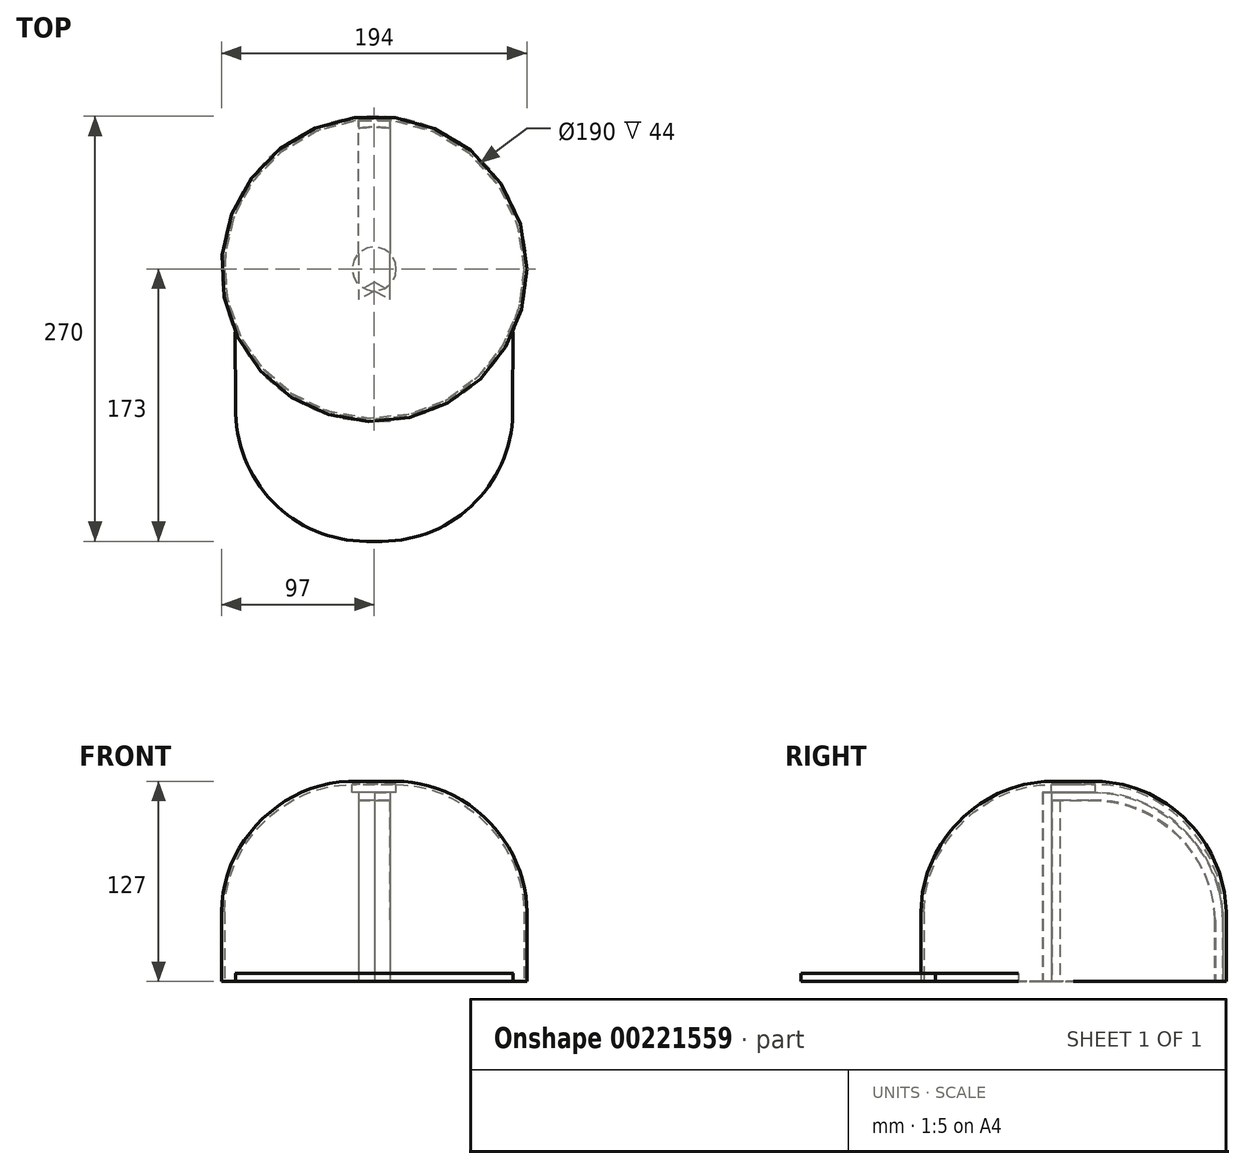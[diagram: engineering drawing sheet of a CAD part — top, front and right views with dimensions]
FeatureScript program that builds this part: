
annotation { "Feature Type Name" : "Feature", "Feature Type Description" : "" }
export const myFeature = defineFeature(function(context is Context, id is Id, definition is map)
    precondition{}
    {
        {
            var Q0;
            Q0=qCreatedBy(makeId("Top.planeOp"),FACE);
            var sketch = newSketch(context, id + "F0", { "sketchPlane" : qUnion([Q0])});
            skCircle(sketch, "E0", {"center": v(0, 0) * mm, "radius": 95 * mm});
            skLineSegment(sketch, "E1", {"start": v(0, -95) * mm, "end": v(0, -35) * mm});
            skLineSegment(sketch, "E2", {"start": v(0, -95) * mm, "end": v(0, -173) * mm});
            skLineSegment(sketch, "E3", {"start": v(0, -173) * mm, "end": v(5, -173) * mm});
            skPoint(sketch, "E4.visualSharp", {"position": v(95, -173) * mm});
            skArc(sketch, "E4.filletArc", {"start": v(5, -173) * mm, "mid": v(64.5, -147.88) * mm, "end": v(87.97, -87.71) * mm});
            skLineSegment(sketch, "E5", {"start": v(87.97, -87.71) * mm, "end": v(88.32, -35) * mm});
            skPoint(sketch, "E6.MirrorP", {"position": v(-95, -173) * mm});
            skLineSegment(sketch, "E7.MirrorCS", {"start": v(-87.97, -87.71) * mm, "end": v(-88.32, -35) * mm});
            skArc(sketch, "E8.MirrorCS", {"start": v(-5, -173) * mm, "mid": v(-64.5, -147.88) * mm, "end": v(-87.97, -87.71) * mm});
            skLineSegment(sketch, "E9.MirrorCS", {"start": v(0, -173) * mm, "end": v(-5, -173) * mm});
            skLineSegment(sketch, "E10", {"start": v(0, 95) * mm, "end": v(0, 0) * mm});
            skLineSegment(sketch, "E11", {"start": v(-85.03, 42.37) * mm, "end": v(0, 0) * mm});
            skLineSegment(sketch, "E12", {"start": v(-82.22, -47.59) * mm, "end": v(0, 0) * mm});
            skLineSegment(sketch, "E13", {"start": v(0, -95) * mm, "end": v(0, 0) * mm});
            skLineSegment(sketch, "E14.MirrorCS", {"start": v(85.03, 42.37) * mm, "end": v(0, 0) * mm});
            skLineSegment(sketch, "E15.MirrorCS", {"start": v(82.22, -47.59) * mm, "end": v(0, 0) * mm});
            skSolve(sketch);
        }
        {
            var Q0;
            {var subQ3=sQuery(id+"F0.wireOp",EDGE,"E12");Q0=makeQuery(id+"F0.imprint","IMPRINT",FACE,{"disambiguationData":[TD([[makeQuery(id+"F0.imprint","IMPRINT",EDGE,{"derivedFrom":subQ3}),-1.0]])]});}
            var Q1;
            {var subQ2=sQuery(id+"F0.wireOp",EDGE,"E11");Q1=makeQuery(id+"F0.imprint","IMPRINT",FACE,{"disambiguationData":[TD([[makeQuery(id+"F0.imprint","IMPRINT",EDGE,{"derivedFrom":subQ2}),-1.0]])]});}
            var Q2;
            {var subQ0=sQuery(id+"F0.wireOp",EDGE,"E10");Q2=makeQuery(id+"F0.imprint","IMPRINT",FACE,{"disambiguationData":[TD([[makeQuery(id+"F0.imprint","IMPRINT",EDGE,{"derivedFrom":subQ0}),-1.0]])]});}
            var Q3;
            {var subQ0=sQuery(id+"F0.wireOp",EDGE,"E10");Q3=makeQuery(id+"F0.imprint","IMPRINT",FACE,{"disambiguationData":[TD([[makeQuery(id+"F0.imprint","IMPRINT",EDGE,{"derivedFrom":subQ0}),1.0]])]});}
            var Q4;
            {var subQ3=sQuery(id+"F0.wireOp",EDGE,"E14.MirrorCS");Q4=makeQuery(id+"F0.imprint","IMPRINT",FACE,{"disambiguationData":[TD([[makeQuery(id+"F0.imprint","IMPRINT",EDGE,{"derivedFrom":subQ3}),1.0]])]});}
            var Q5;
            {var subQ3=sQuery(id+"F0.wireOp",EDGE,"E15.MirrorCS");Q5=makeQuery(id+"F0.imprint","IMPRINT",FACE,{"disambiguationData":[TD([[makeQuery(id+"F0.imprint","IMPRINT",EDGE,{"derivedFrom":subQ3}),1.0]])]});}
            extrude(context, id + "F1", {"entities" : qUnion([Q0, Q1, Q2, Q3, Q4, Q5]), "depth" : 125 * mm});
        }
        {
            var Q0;
            Q0=makeQuery(id+"F1.opExtrude","CAP_EDGE",EDGE,{"disambiguationData":[OSD([sQuery(id+"F0.wireOp",EDGE,"E0")])],"isStart":false});
            fillet(context, id + "F2", {"entities" : qUnion([Q0]), "radius" : 81 * mm, "tangentPropagation" : true, "rho" : 0.4, "crossSection" : FilletCrossSection.CONIC, "allowEdgeOverflow" : false});
        }
        {
            var Q0;
            {var subQ1=sQuery(id+"F0.wireOp",EDGE,"E2");Q0=makeQuery(id+"F0.imprint","IMPRINT",FACE,{"disambiguationData":[TD([[makeQuery(id+"F0.imprint","IMPRINT",EDGE,{"derivedFrom":subQ1}),-1.0]])]});}
            var Q1;
            {var subQ0=sQuery(id+"F0.wireOp",EDGE,"E2");Q1=makeQuery(id+"F0.imprint","IMPRINT",FACE,{"disambiguationData":[TD([[makeQuery(id+"F0.imprint","IMPRINT",EDGE,{"derivedFrom":subQ0}),1.0]])]});}
            extrude(context, id + "F3", {"entities" : qUnion([Q0, Q1]), "depth" : 5 * mm});
        }
        {
            var Q0;
            Q0=makeQuery(id+"F1.opExtrude","CAP_FACE",FACE,{"disambiguationData":[OSD([sQuery(id+"F0.wireOp",EDGE,"E0")])],"isStart":true});
            shell(context, id + "F4", {"entities" : qUnion([Q0]), "thickness" : 2 * mm, "oppositeDirection" : true});
        }
        {
            var Q0;
            {var subQ0=sQuery(id+"F0.wireOp",EDGE,"E0");Q0=makeQuery(id+"F4.opShell","OFFSET_FACE",FACE,{"disambiguationData":[OSD([subQ0]),TDD([makeQuery(id+"F1.opExtrude","CAP_FACE",FACE,{"disambiguationData":[OSD([subQ0])],"isStart":false})])]});}
            extrude(context, id + "F5", {"entities" : qUnion([Q0]), "depth" : 5 * mm});
        }
        {
            var Q0;
            Q0=qCreatedBy(makeId("Top.planeOp"),FACE);
            var sketch = newSketch(context, id + "F6", { "sketchPlane" : qUnion([Q0])});
            skCircle(sketch, "E16", {"center": v(0, 0) * mm, "radius": 95 * mm});
            skLineSegment(sketch, "E17", {"start": v(0, -95) * mm, "end": v(0, -35) * mm});
            skLineSegment(sketch, "E18", {"start": v(0, -95) * mm, "end": v(0, -173) * mm});
            skLineSegment(sketch, "E19", {"start": v(0, -173) * mm, "end": v(5, -173) * mm});
            skPoint(sketch, "E20.visualSharp", {"position": v(95, -173) * mm});
            skArc(sketch, "E20.filletArc", {"start": v(5, -173) * mm, "mid": v(64.5, -147.88) * mm, "end": v(87.97, -87.71) * mm});
            skLineSegment(sketch, "E21", {"start": v(87.97, -87.71) * mm, "end": v(88.32, -35) * mm});
            skPoint(sketch, "E22.MirrorP", {"position": v(-95, -173) * mm});
            skLineSegment(sketch, "E23.MirrorCS", {"start": v(-87.97, -87.71) * mm, "end": v(-88.32, -35) * mm});
            skArc(sketch, "E24.MirrorCS", {"start": v(-5, -173) * mm, "mid": v(-64.5, -147.88) * mm, "end": v(-87.97, -87.71) * mm});
            skLineSegment(sketch, "E25.MirrorCS", {"start": v(0, -173) * mm, "end": v(-5, -173) * mm});
            skLineSegment(sketch, "E26", {"start": v(0, 95) * mm, "end": v(0, 0) * mm});
            skLineSegment(sketch, "E27", {"start": v(-85.03, 42.37) * mm, "end": v(0, 0) * mm});
            skLineSegment(sketch, "E28", {"start": v(-82.22, -47.59) * mm, "end": v(0, 0) * mm});
            skLineSegment(sketch, "E29", {"start": v(0, -95) * mm, "end": v(0, 0) * mm});
            skLineSegment(sketch, "E30.MirrorCS", {"start": v(85.03, 42.37) * mm, "end": v(0, 0) * mm});
            skLineSegment(sketch, "E31.MirrorCS", {"start": v(82.22, -47.59) * mm, "end": v(0, 0) * mm});
            skLineSegment(sketch, "E32", {"start": v(-88.77, 33.85) * mm, "end": v(77, -55.64) * mm});
            skLineSegment(sketch, "E33", {"start": v(-79.71, 51.68) * mm, "end": v(86.94, -38.3) * mm});
            skLineSegment(sketch, "E34", {"start": v(86.94, -38.3) * mm, "end": v(77, -55.64) * mm});
            skLineSegment(sketch, "E35", {"start": v(-88.77, 33.85) * mm, "end": v(-79.71, 51.68) * mm});
            skLineSegment(sketch, "E36", {"start": v(88.82, 33.71) * mm, "end": v(-76.93, -55.74) * mm});
            skLineSegment(sketch, "E37", {"start": v(79.8, 51.56) * mm, "end": v(-86.9, -38.4) * mm});
            skLineSegment(sketch, "E38", {"start": v(79.8, 51.56) * mm, "end": v(88.82, 33.71) * mm});
            skLineSegment(sketch, "E39", {"start": v(-76.93, -55.74) * mm, "end": v(-86.9, -38.4) * mm});
            skLineSegment(sketch, "E40", {"start": v(-10, 94.47) * mm, "end": v(-10, -94.47) * mm});
            skLineSegment(sketch, "E41", {"start": v(-10, -94.47) * mm, "end": v(10, -94.47) * mm});
            skLineSegment(sketch, "E42", {"start": v(10, -94.47) * mm, "end": v(10, 94.47) * mm});
            skLineSegment(sketch, "E43", {"start": v(10, 94.47) * mm, "end": v(-10, 94.47) * mm});
            skSolve(sketch);
        }
        {
            var Q0;
            {var subQ0=sQuery(id+"F6.wireOp",EDGE,"E43");var subQ1=sQuery(id+"F6.wireOp",EDGE,"E26");var subQ2=makeQuery(id+"F6.imprint","INTERSECT",VERTEX,{"derivedFrom":[subQ1,subQ0]});Q0=makeQuery(id+"F6.imprint","IMPRINT",FACE,{"disambiguationData":[TD([[makeQuery(id+"F6.imprint","IMPRINT",EDGE,{"disambiguationData":[TD([[subQ2,-1.0]])],"derivedFrom":subQ1}),-1.0]])]});}
            var Q1;
            {var subQ0=sQuery(id+"F6.wireOp",EDGE,"E43");var subQ7=sQuery(id+"F6.wireOp",EDGE,"E26");var subQ9=makeQuery(id+"F6.imprint","INTERSECT",VERTEX,{"derivedFrom":[subQ7,subQ0]});Q1=makeQuery(id+"F6.imprint","IMPRINT",FACE,{"disambiguationData":[TD([[makeQuery(id+"F6.imprint","IMPRINT",EDGE,{"disambiguationData":[TD([[subQ9,-1.0]])],"derivedFrom":subQ7}),1.0]])]});}
            var Q2;
            {var subQ5=sQuery(id+"F6.wireOp",EDGE,"E29");var subQ7=makeQuery(id+"F6.imprint","IMPRINT",VERTEX,{"derivedFrom":subQ5});Q2=makeQuery(id+"F6.imprint","IMPRINT",FACE,{"disambiguationData":[TD([[makeQuery(id+"F6.imprint","IMPRINT",EDGE,{"disambiguationData":[TD([[subQ7,1.0]])],"derivedFrom":subQ5}),-1.0]])]});}
            var Q3;
            {var subQ5=sQuery(id+"F6.wireOp",EDGE,"E29");var subQ7=makeQuery(id+"F6.imprint","IMPRINT",VERTEX,{"derivedFrom":subQ5});Q3=makeQuery(id+"F6.imprint","IMPRINT",FACE,{"disambiguationData":[TD([[makeQuery(id+"F6.imprint","IMPRINT",EDGE,{"disambiguationData":[TD([[subQ7,1.0]])],"derivedFrom":subQ5}),1.0]])]});}
            var Q4;
            {var subQ0=sQuery(id+"F6.wireOp",EDGE,"E26");var subQ1=sQuery(id+"F6.wireOp",EDGE,"E16");var subQ2=makeQuery(id+"F6.imprint","INTERSECT",VERTEX,{"derivedFrom":[subQ1,subQ0]});Q4=makeQuery(id+"F6.imprint","IMPRINT",FACE,{"disambiguationData":[TD([[makeQuery(id+"F6.imprint","IMPRINT",EDGE,{"disambiguationData":[TD([[subQ2,-1.0]])],"derivedFrom":subQ0}),1.0]])]});}
            var Q5;
            {var subQ0=sQuery(id+"F6.wireOp",EDGE,"E26");var subQ1=sQuery(id+"F6.wireOp",EDGE,"E16");var subQ2=makeQuery(id+"F6.imprint","INTERSECT",VERTEX,{"derivedFrom":[subQ1,subQ0]});Q5=makeQuery(id+"F6.imprint","IMPRINT",FACE,{"disambiguationData":[TD([[makeQuery(id+"F6.imprint","IMPRINT",EDGE,{"disambiguationData":[TD([[subQ2,-1.0]])],"derivedFrom":subQ0}),-1.0]])]});}
            var Q6;
            {var subQ0=sQuery(id+"F6.wireOp",EDGE,"E29");var subQ3=sQuery(id+"F6.wireOp",EDGE,"E41");var subQ5=makeQuery(id+"F6.imprint","INTERSECT",VERTEX,{"derivedFrom":[subQ0,subQ3]});Q6=makeQuery(id+"F6.imprint","IMPRINT",FACE,{"disambiguationData":[TD([[makeQuery(id+"F6.imprint","IMPRINT",EDGE,{"disambiguationData":[TD([[subQ5,1.0]])],"derivedFrom":subQ0}),1.0]])]});}
            var Q7;
            {var subQ0=sQuery(id+"F6.wireOp",EDGE,"E29");var subQ3=sQuery(id+"F6.wireOp",EDGE,"E41");var subQ5=makeQuery(id+"F6.imprint","INTERSECT",VERTEX,{"derivedFrom":[subQ0,subQ3]});Q7=makeQuery(id+"F6.imprint","IMPRINT",FACE,{"disambiguationData":[TD([[makeQuery(id+"F6.imprint","IMPRINT",EDGE,{"disambiguationData":[TD([[subQ5,1.0]])],"derivedFrom":subQ0}),-1.0]])]});}
            var Q8;
            {var subQ0=sQuery(id+"F6.wireOp",EDGE,"E42");var subQ1=sQuery(id+"F6.wireOp",EDGE,"E30.MirrorCS");var subQ2=makeQuery(id+"F6.imprint","INTERSECT",VERTEX,{"derivedFrom":[subQ1,subQ0]});Q8=makeQuery(id+"F6.imprint","IMPRINT",FACE,{"disambiguationData":[TD([[makeQuery(id+"F6.imprint","IMPRINT",EDGE,{"disambiguationData":[TD([[subQ2,-1.0]])],"derivedFrom":subQ1}),-1.0]])]});}
            var Q9;
            {var subQ0=sQuery(id+"F6.wireOp",EDGE,"E30.MirrorCS");var subQ5=sQuery(id+"F6.wireOp",EDGE,"E33");var subQ6=makeQuery(id+"F6.imprint","INTERSECT",VERTEX,{"derivedFrom":[subQ0,subQ5]});Q9=makeQuery(id+"F6.imprint","IMPRINT",FACE,{"disambiguationData":[TD([[makeQuery(id+"F6.imprint","IMPRINT",EDGE,{"disambiguationData":[TD([[subQ6,1.0]])],"derivedFrom":subQ5}),-1.0]])]});}
            var Q10;
            {var subQ1=sQuery(id+"F6.wireOp",EDGE,"E26");var subQ3=sQuery(id+"F6.wireOp",EDGE,"E37");var subQ4=makeQuery(id+"F6.imprint","INTERSECT",VERTEX,{"derivedFrom":[subQ1,subQ3]});Q10=makeQuery(id+"F6.imprint","IMPRINT",FACE,{"disambiguationData":[TD([[makeQuery(id+"F6.imprint","IMPRINT",EDGE,{"disambiguationData":[TD([[subQ4,-1.0]])],"derivedFrom":subQ3}),1.0]])]});}
            var Q11;
            {var subQ1=sQuery(id+"F6.wireOp",EDGE,"E26");var subQ5=sQuery(id+"F6.wireOp",EDGE,"E33");var subQ6=makeQuery(id+"F6.imprint","INTERSECT",VERTEX,{"derivedFrom":[subQ1,subQ5]});Q11=makeQuery(id+"F6.imprint","IMPRINT",FACE,{"disambiguationData":[TD([[makeQuery(id+"F6.imprint","IMPRINT",EDGE,{"disambiguationData":[TD([[subQ6,-1.0]])],"derivedFrom":subQ1}),-1.0]])]});}
            var Q12;
            {var subQ0=sQuery(id+"F6.wireOp",EDGE,"E36");var subQ1=sQuery(id+"F6.wireOp",EDGE,"E32");var subQ2=makeQuery(id+"F6.imprint","INTERSECT",VERTEX,{"derivedFrom":[subQ1,subQ0]});Q12=makeQuery(id+"F6.imprint","IMPRINT",FACE,{"disambiguationData":[TD([[makeQuery(id+"F6.imprint","IMPRINT",EDGE,{"disambiguationData":[TD([[subQ2,-1.0]])],"derivedFrom":subQ1}),1.0]])]});}
            var Q13;
            {var subQ0=sQuery(id+"F6.wireOp",EDGE,"E36");var subQ1=sQuery(id+"F6.wireOp",EDGE,"E29");var subQ2=makeQuery(id+"F6.imprint","INTERSECT",VERTEX,{"derivedFrom":[subQ1,subQ0]});Q13=makeQuery(id+"F6.imprint","IMPRINT",FACE,{"disambiguationData":[TD([[makeQuery(id+"F6.imprint","IMPRINT",EDGE,{"disambiguationData":[TD([[subQ2,-1.0]])],"derivedFrom":subQ1}),1.0]])]});}
            var Q14;
            {var subQ0=sQuery(id+"F6.wireOp",EDGE,"E29");var subQ5=sQuery(id+"F6.wireOp",EDGE,"E32");var subQ6=makeQuery(id+"F6.imprint","INTERSECT",VERTEX,{"derivedFrom":[subQ0,subQ5]});Q14=makeQuery(id+"F6.imprint","IMPRINT",FACE,{"disambiguationData":[TD([[makeQuery(id+"F6.imprint","IMPRINT",EDGE,{"disambiguationData":[TD([[subQ6,1.0]])],"derivedFrom":subQ5}),1.0]])]});}
            var Q15;
            {var subQ0=sQuery(id+"F6.wireOp",EDGE,"E32");var subQ1=sQuery(id+"F6.wireOp",EDGE,"E29");var subQ2=makeQuery(id+"F6.imprint","INTERSECT",VERTEX,{"derivedFrom":[subQ1,subQ0]});Q15=makeQuery(id+"F6.imprint","IMPRINT",FACE,{"disambiguationData":[TD([[makeQuery(id+"F6.imprint","IMPRINT",EDGE,{"disambiguationData":[TD([[subQ2,-1.0]])],"derivedFrom":subQ0}),1.0]])]});}
            var Q16;
            {var subQ1=sQuery(id+"F6.wireOp",EDGE,"E30.MirrorCS");var subQ3=sQuery(id+"F6.wireOp",EDGE,"E33");var subQ4=makeQuery(id+"F6.imprint","INTERSECT",VERTEX,{"derivedFrom":[subQ1,subQ3]});Q16=makeQuery(id+"F6.imprint","IMPRINT",FACE,{"disambiguationData":[TD([[makeQuery(id+"F6.imprint","IMPRINT",EDGE,{"disambiguationData":[TD([[subQ4,-1.0]])],"derivedFrom":subQ3}),-1.0]])]});}
            var Q17;
            {var subQ1=sQuery(id+"F6.wireOp",EDGE,"E27");var subQ3=sQuery(id+"F6.wireOp",EDGE,"E37");var subQ4=makeQuery(id+"F6.imprint","INTERSECT",VERTEX,{"derivedFrom":[subQ1,subQ3]});Q17=makeQuery(id+"F6.imprint","IMPRINT",FACE,{"disambiguationData":[TD([[makeQuery(id+"F6.imprint","IMPRINT",EDGE,{"disambiguationData":[TD([[subQ4,-1.0]])],"derivedFrom":subQ3}),1.0]])]});}
            var Q18;
            {var subQ0=sQuery(id+"F6.wireOp",EDGE,"E40");var subQ1=sQuery(id+"F6.wireOp",EDGE,"E27");var subQ2=makeQuery(id+"F6.imprint","INTERSECT",VERTEX,{"derivedFrom":[subQ1,subQ0]});Q18=makeQuery(id+"F6.imprint","IMPRINT",FACE,{"disambiguationData":[TD([[makeQuery(id+"F6.imprint","IMPRINT",EDGE,{"disambiguationData":[TD([[subQ2,-1.0]])],"derivedFrom":subQ1}),-1.0]])]});}
            var Q19;
            {var subQ0=sQuery(id+"F6.wireOp",EDGE,"E42");var subQ1=sQuery(id+"F6.wireOp",EDGE,"E30.MirrorCS");var subQ2=makeQuery(id+"F6.imprint","INTERSECT",VERTEX,{"derivedFrom":[subQ1,subQ0]});Q19=makeQuery(id+"F6.imprint","IMPRINT",FACE,{"disambiguationData":[TD([[makeQuery(id+"F6.imprint","IMPRINT",EDGE,{"disambiguationData":[TD([[subQ2,-1.0]])],"derivedFrom":subQ1}),1.0]])]});}
            var Q20;
            {var subQ0=sQuery(id+"F6.wireOp",EDGE,"E36");var subQ1=sQuery(id+"F6.wireOp",EDGE,"E29");var subQ2=makeQuery(id+"F6.imprint","INTERSECT",VERTEX,{"derivedFrom":[subQ1,subQ0]});Q20=makeQuery(id+"F6.imprint","IMPRINT",FACE,{"disambiguationData":[TD([[makeQuery(id+"F6.imprint","IMPRINT",EDGE,{"disambiguationData":[TD([[subQ2,-1.0]])],"derivedFrom":subQ1}),-1.0]])]});}
            var Q21;
            {var subQ0=sQuery(id+"F6.wireOp",EDGE,"E33");var subQ1=sQuery(id+"F6.wireOp",EDGE,"E26");var subQ2=makeQuery(id+"F6.imprint","INTERSECT",VERTEX,{"derivedFrom":[subQ1,subQ0]});Q21=makeQuery(id+"F6.imprint","IMPRINT",FACE,{"disambiguationData":[TD([[makeQuery(id+"F6.imprint","IMPRINT",EDGE,{"disambiguationData":[TD([[subQ2,-1.0]])],"derivedFrom":subQ1}),1.0]])]});}
            extrude(context, id + "F7", {"entities" : qUnion([Q0, Q1, Q2, Q3, Q4, Q5, Q6, Q7, Q8, Q9, Q10, Q11, Q12, Q13, Q14, Q15, Q16, Q17, Q18, Q19, Q20, Q21]), "depth" : 120 * mm});
        }
        {
            var Q0;
            {var subQ0=sQuery(id+"F6.wireOp",EDGE,"E16");var subQ1=makeQuery(id+"F6.imprint","INTERSECT",VERTEX,{"derivedFrom":[subQ0,sQuery(id+"F6.wireOp",EDGE,"E26")]});Q0=makeQuery(id+"F7.opExtrude","CAP_EDGE",EDGE,{"disambiguationData":[OSD([subQ0]),TDD([makeQuery(id+"F6.imprint","IMPRINT",EDGE,{"disambiguationData":[TD([[subQ1,1.0]])],"derivedFrom":subQ0}),makeQuery(id+"F6.imprint","IMPRINT",EDGE,{"disambiguationData":[TD([[subQ1,-1.0]])],"derivedFrom":subQ0})])],"isStart":false});}
            var Q1;
            {var subQ0=sQuery(id+"F6.wireOp",EDGE,"E16");var subQ1=makeQuery(id+"F6.imprint","INTERSECT",VERTEX,{"derivedFrom":[subQ0,sQuery(id+"F6.wireOp",EDGE,"E18"),sQuery(id+"F6.wireOp",EDGE,"E29")]});Q1=makeQuery(id+"F7.opExtrude","CAP_EDGE",EDGE,{"disambiguationData":[OSD([subQ0]),TDD([makeQuery(id+"F6.imprint","IMPRINT",EDGE,{"disambiguationData":[TD([[subQ1,1.0]])],"derivedFrom":subQ0}),makeQuery(id+"F6.imprint","IMPRINT",EDGE,{"disambiguationData":[TD([[subQ1,-1.0]])],"derivedFrom":subQ0})])],"isStart":false});}
            fillet(context, id + "F8", {"entities" : qUnion([Q0, Q1]), "radius" : 81 * mm, "tangentPropagation" : true, "rho" : 0.4, "crossSection" : FilletCrossSection.CONIC, "allowEdgeOverflow" : false});
        }
        {
            var Q0;
            Q0=makeQuery(id+"F7.opExtrude","SWEPT_FACE",FACE,{"disambiguationData":[OSD([sQuery(id+"F6.wireOp",EDGE,"E40")])]});
            var Q1;
            Q1=makeQuery(id+"F7.opExtrude","SWEPT_FACE",FACE,{"disambiguationData":[OSD([sQuery(id+"F6.wireOp",EDGE,"E42")])]});
            shell(context, id + "F9", {"entities" : qUnion([Q0, Q1]), "thickness" : 5 * mm});
        }
        {
            var Q0;
            {var subQ0=sQuery(id+"F6.wireOp",EDGE,"E42");var subQ1=sQuery(id+"F6.wireOp",EDGE,"E40");var subQ2=sQuery(id+"F6.wireOp",EDGE,"E16");Q0=makeQuery(id+"F9.opShell","OFFSET_FACE",FACE,{"disambiguationData":[OSD([subQ2,subQ1,subQ0]),TDD([makeQuery(id+"F7.opExtrude","CAP_FACE",FACE,{"disambiguationData":[OSD([subQ2,subQ1,subQ0])],"isStart":true})])]});}
            extrude(context, id + "F10", {"entities" : qUnion([Q0]), "operationType" : NewBodyOperationType.REMOVE, "oppositeDirection" : true, "depth" : 25 * mm});
        }
    });
